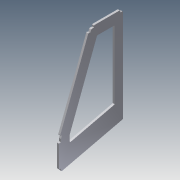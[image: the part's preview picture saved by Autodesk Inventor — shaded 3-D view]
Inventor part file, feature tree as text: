
AUTODESK INVENTOR PART (.ipt)
format: ipt  version: 2014 (Build 180170000, 170)  size: 188,416 bytes
history: native  units: mm
features: extrude x7, sketch x7, fillet x3
ambient origin geometry x8: Origin, YZ Plane, XZ Plane, XY Plane, X Axis, Y Axis, Z Axis, Center Point
bodies: Solid1 (feature_tree)
feature tree (17):
  extrude  "Extrusion1"  Depth=186.0mm
  extrude  "Extrusion2"  Depth=95.0mm
  extrude  "Extrusion3"  Depth=6.0mm
  extrude  "Extrusion6"  Depth=6.0mm
  fillet  "Fillet2"  Radius=8.1mm
  fillet  "Fillet3"  Radius=8.1mm
  extrude  "Extrusion4"  Depth=3.0mm
  extrude  "Extrusion7"  Depth=25.0mm
  extrude  "Extrusion8"  Depth=25.0mm
  fillet  "Fillet4"  Radius=4.0mm
  sketch  "Sketch1"  dims[d0=325.0mm d1=186.0mm]
  sketch  "Sketch2"  dims[d2=85.0mm d3=95.0mm]
  sketch  "Sketch3"  dims[d4=6.0mm d5=0.0mm d6=6.0mm]
  sketch  "Sketch4"  dims[d9=6.0mm d10=0.0mm d12=6.0mm d13=8.1mm d17=8.1mm]
  sketch  "Sketch6"  dims[d20=6.0mm d21=0.0mm d22=3.0mm]
  sketch  "Sketch7"  dims[d23=2.0mm d24=25.0mm]
  sketch  "Sketch8"  dims[d26=25.0mm d27=25.0mm d29=4.0mm d30=0.0mm d33=240.0mm d34=91.0mm d35=6.0mm d36=8.1mm d38=50.0mm d39=25.0mm d40=10.0mm d41=0.0mm d42=10.0mm d43=0.0mm d44=10.0mm d45=6.0mm d46=0.0mm d47=8.1mm d48=8.1mm d49=2.0mm]
